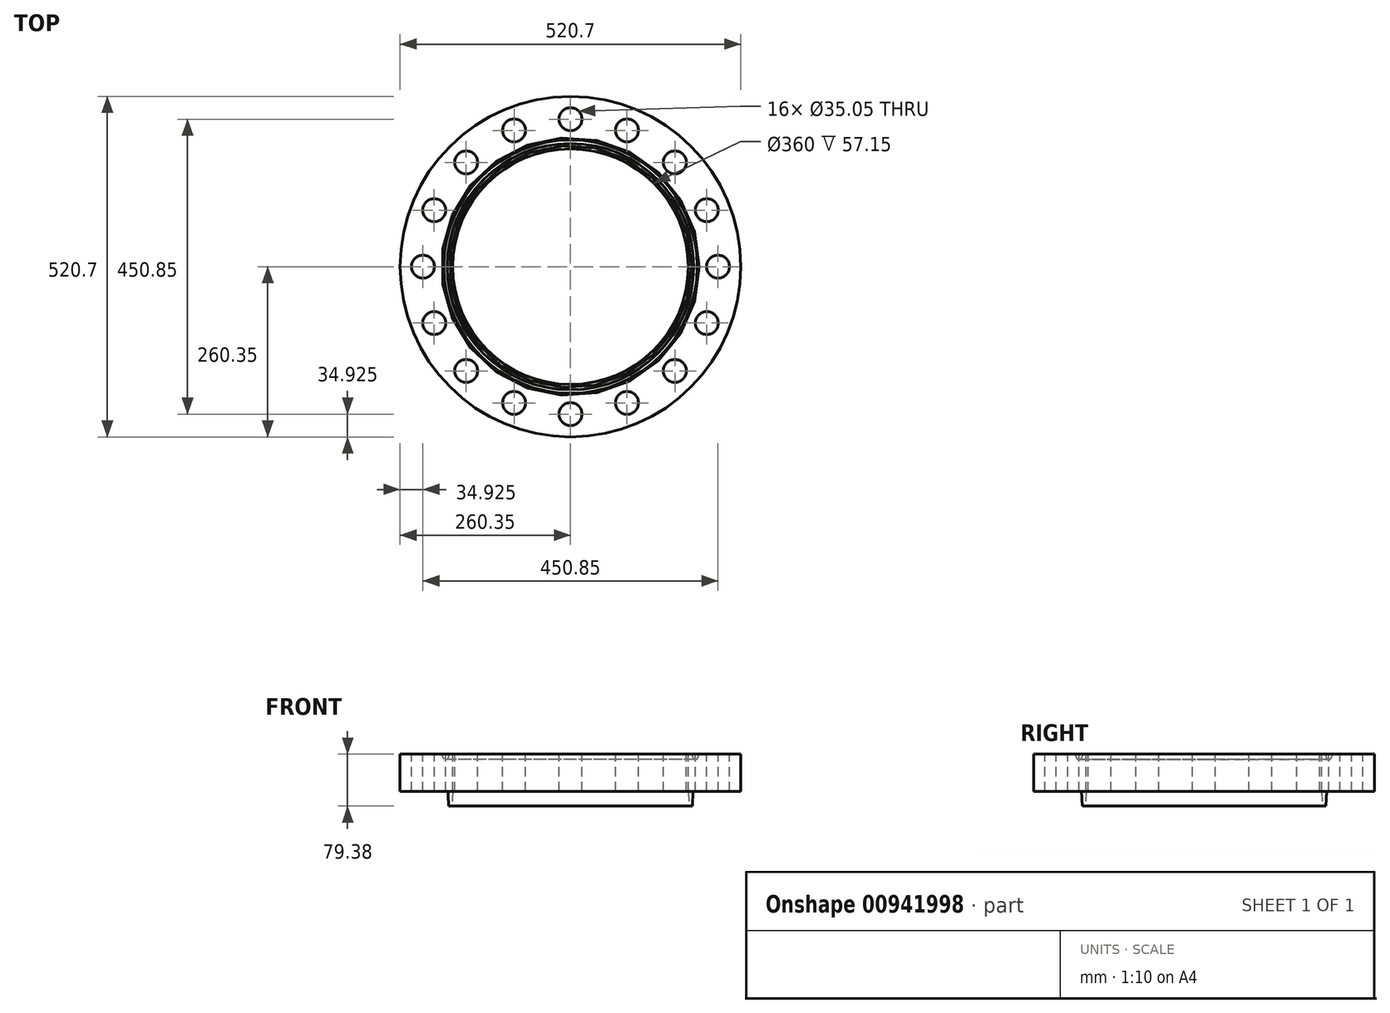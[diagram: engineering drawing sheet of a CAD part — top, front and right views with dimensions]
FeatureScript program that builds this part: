
annotation { "Feature Type Name" : "Feature", "Feature Type Description" : "" }
export const myFeature = defineFeature(function(context is Context, id is Id, definition is map)
    precondition{}
    {
        {
            var Q0;
            Q0=qCreatedBy(makeId("Top.planeOp"),FACE);
            var sketch = newSketch(context, id + "F0", { "sketchPlane" : qUnion([Q0])});
            skCircle(sketch, "E0", {"center": v(0, 0) * mm, "radius": 260.35 * mm});
            skSolve(sketch);
        }
        {
            var Q0;
            Q0=makeQuery(id+"F0.imprint","IMPRINT",FACE,{"disambiguationData":[TD([[makeQuery(id+"F0.imprint","IMPRINT",EDGE,{"derivedFrom":sQuery(id+"F0.wireOp",EDGE,"E0")}),1.0]])]});
            extrude(context, id + "F1", {"entities" : qUnion([Q0]), "depth" : 57.15 * mm, "offsetDistance" : 25 * mm});
        }
        {
            var Q0;
            Q0=makeQuery(id+"F1.opExtrude","CAP_FACE",FACE,{"disambiguationData":[OSD([sQuery(id+"F0.wireOp",EDGE,"E0")])],"isStart":false});
            var sketch = newSketch(context, id + "F2", { "sketchPlane" : qUnion([Q0])});
            skCircle(sketch, "E1", {"center": v(0, 0) * mm, "radius": 180 * mm});
            skSolve(sketch);
        }
        {
            var Q0;
            Q0 = qSketchRegion(id + "F2", true);
            extrude(context, id + "F3", {"entities" : qUnion([Q0]), "operationType" : NewBodyOperationType.REMOVE, "endBound" : BoundingType.THROUGH_ALL, "oppositeDirection" : true, "depth" : 25 * mm, "offsetDistance" : 25 * mm});
        }
        {
            var Q0;
            Q0=makeQuery(id+"F1.opExtrude","CAP_FACE",FACE,{"disambiguationData":[OSD([sQuery(id+"F0.wireOp",EDGE,"E0")])],"isStart":true});
            var sketch = newSketch(context, id + "F4", { "sketchPlane" : qUnion([Q0])});
            skCircle(sketch, "E2", {"center": v(0, 0) * mm, "radius": 187.32 * mm});
            skSolve(sketch);
        }
        {
            var Q0;
            Q0=makeQuery(id+"F4.imprint","IMPRINT",FACE,{"disambiguationData":[TD([[makeQuery(id+"F4.imprint","IMPRINT",EDGE,{"derivedFrom":sQuery(id+"F4.wireOp",EDGE,"E2")}),1.0]])]});
            extrude(context, id + "F5", {"entities" : qUnion([Q0]), "operationType" : NewBodyOperationType.ADD, "depth" : 22.23 * mm, "offsetDistance" : 25 * mm, "hasDraft" : true, "draftAngle" : 3 * degree, "draftPullDirection" : true});
        }
        {
            var Q0;
            Q0=makeQuery(id+"F1.opExtrude","CAP_FACE",FACE,{"disambiguationData":[OSD([sQuery(id+"F0.wireOp",EDGE,"E0")])],"isStart":false});
            var sketch = newSketch(context, id + "F6", { "sketchPlane" : qUnion([Q0])});
            skCircle(sketch, "E3", {"center": v(0, 0) * mm, "radius": 190.5 * mm});
            skPoint(sketch, "E4", {"position": v(190.5, 0) * mm});
            skSolve(sketch);
        }
        {
            var Q0;
            Q0=qCreatedBy(makeId("Front.planeOp"),FACE);
            var sketch = newSketch(context, id + "F7", { "sketchPlane" : qUnion([Q0])});
            skLineSegment(sketch, "E5", {"start": v(190.9, 57.15) * mm, "end": v(196.85, 57.15) * mm});
            skLineSegment(sketch, "E6", {"start": v(190.9, 57.15) * mm, "end": v(184.94, 57.15) * mm});
            skLineSegment(sketch, "E7", {"start": v(190.9, 57.15) * mm, "end": v(190.9, 49.21) * mm});
            skLineSegment(sketch, "E8", {"start": v(184.94, 57.15) * mm, "end": v(188.3, 49.21) * mm});
            skLineSegment(sketch, "E9.MirrorCS", {"start": v(196.85, 57.15) * mm, "end": v(193.48, 49.21) * mm});
            skLineSegment(sketch, "E10", {"start": v(188.3, 49.21) * mm, "end": v(193.48, 49.21) * mm});
            skSolve(sketch);
        }
        {
            var Q0;
            Q0 = qSketchRegion(id + "F7", true);
            var Q1;
            Q1=sQuery(id+"F6.wireOp",EDGE,"E3");
            revolve(context, id + "F8", {"operationType" : NewBodyOperationType.REMOVE, "surfaceOperationType" : NewSurfaceOperationType.NEW, "entities" : qUnion([Q0]), "axis" : qUnion([Q1]), "revolveType" : RevolveType.FULL, "oppositeDirection" : true});
        }
        {
            var Q0;
            {var subQ0=sQuery(id+"F0.wireOp",EDGE,"E0");Q0=makeQuery(id+"F8.boolean.opBoolean","SPLIT",FACE,{"disambiguationData":[TD([makeQuery(id+"F1.opExtrude","SWEPT_FACE",FACE,{"disambiguationData":[OSD([subQ0])]})])],"derivedFrom":makeQuery(id+"F1.opExtrude","CAP_FACE",FACE,{"disambiguationData":[OSD([subQ0])],"isStart":false})});}
            var sketch = newSketch(context, id + "F9", { "sketchPlane" : qUnion([Q0])});
            skPoint(sketch, "E11", {"position": v(225.42, 0) * mm});
            skPoint(sketch, "E12.1.0", {"position": v(208.27, 86.27) * mm});
            skPoint(sketch, "E12.2.0", {"position": v(159.4, 159.4) * mm});
            skPoint(sketch, "E12.3.0", {"position": v(86.27, 208.27) * mm});
            skPoint(sketch, "E12.4.0", {"position": v(0, 225.42) * mm});
            skPoint(sketch, "E12.5.0", {"position": v(-86.27, 208.27) * mm});
            skPoint(sketch, "E12.6.0", {"position": v(-159.4, 159.4) * mm});
            skPoint(sketch, "E12.7.0", {"position": v(-208.27, 86.27) * mm});
            skPoint(sketch, "E12.8.0", {"position": v(-225.42, 0) * mm});
            skPoint(sketch, "E12.9.0", {"position": v(-208.27, -86.27) * mm});
            skPoint(sketch, "E12.10.0", {"position": v(-159.4, -159.4) * mm});
            skPoint(sketch, "E12.11.0", {"position": v(-86.27, -208.27) * mm});
            skPoint(sketch, "E12.12.0", {"position": v(0, -225.42) * mm});
            skPoint(sketch, "E12.13.0", {"position": v(86.27, -208.27) * mm});
            skPoint(sketch, "E12.14.0", {"position": v(159.4, -159.4) * mm});
            skPoint(sketch, "E12.15.0", {"position": v(208.27, -86.27) * mm});
            skPoint(sketch, "E12.center", {"position": v(0, 0) * mm});
            skSolve(sketch);
        }
        {
            var Q0;
            Q0=sQuery(id+"F9.wireOp",VERTEX,"E11");
            var Q1;
            Q1=sQuery(id+"F9.wireOp",VERTEX,"E12.15.0");
            var Q2;
            Q2=sQuery(id+"F9.wireOp",VERTEX,"E12.14.0");
            var Q3;
            Q3=sQuery(id+"F9.wireOp",VERTEX,"E12.13.0");
            var Q4;
            Q4=sQuery(id+"F9.wireOp",VERTEX,"E12.12.0");
            var Q5;
            Q5=sQuery(id+"F9.wireOp",VERTEX,"E12.11.0");
            var Q6;
            Q6=sQuery(id+"F9.wireOp",VERTEX,"E12.10.0");
            var Q7;
            Q7=sQuery(id+"F9.wireOp",VERTEX,"E12.9.0");
            var Q8;
            Q8=sQuery(id+"F9.wireOp",VERTEX,"E12.8.0");
            var Q9;
            Q9=sQuery(id+"F9.wireOp",VERTEX,"E12.7.0");
            var Q10;
            Q10=sQuery(id+"F9.wireOp",VERTEX,"E12.6.0");
            var Q11;
            Q11=sQuery(id+"F9.wireOp",VERTEX,"E12.5.0");
            var Q12;
            Q12=sQuery(id+"F9.wireOp",VERTEX,"E12.4.0");
            var Q13;
            Q13=sQuery(id+"F9.wireOp",VERTEX,"E12.3.0");
            var Q14;
            Q14=sQuery(id+"F9.wireOp",VERTEX,"E12.2.0");
            var Q15;
            Q15=sQuery(id+"F9.wireOp",VERTEX,"E12.1.0");
            var Q16;
            Q16=makeQuery(id+"F1.opExtrude","SWEPT_BODY",BODY,{"disambiguationData":[OSD([sQuery(id+"F0.wireOp",EDGE,"E0")])]});
            hole(context, id + "F10", {"style" : HoleStyle.SIMPLE, "endStyle" : HoleEndStyle.THROUGH, "holeDiameter" : 35.05 * mm, "majorDiameter" : 5 * mm, "isTappedThrough" : true, "tappedDepth" : 12 * mm, "tapClearance" : 3, "locations" : qUnion([Q0, Q1, Q2, Q3, Q4, Q5, Q6, Q7, Q8, Q9, Q10, Q11, Q12, Q13, Q14, Q15]), "scope" : qUnion([Q16])});
        }
    });
